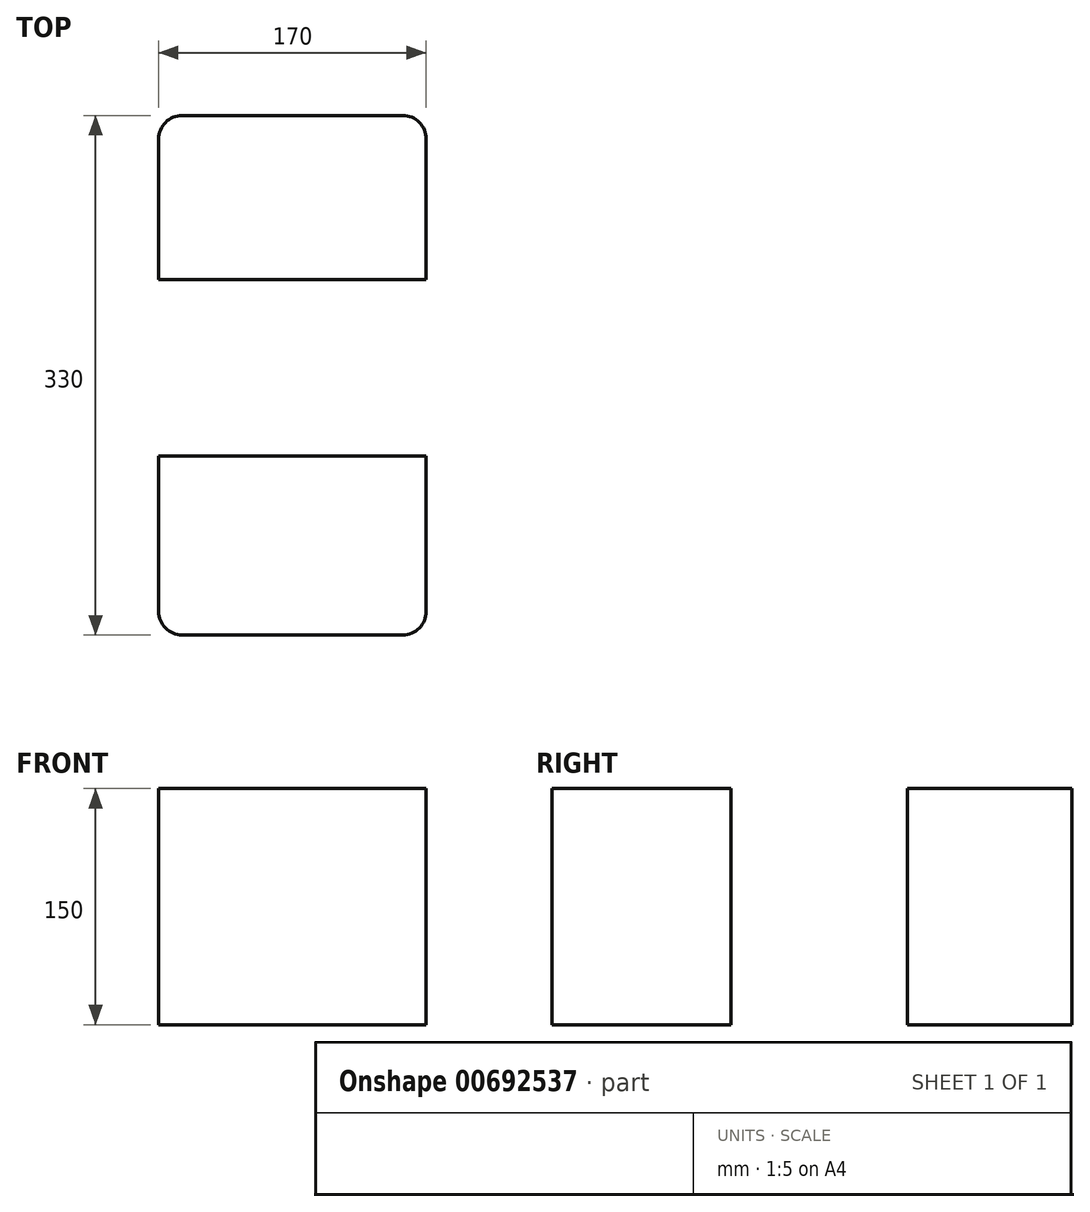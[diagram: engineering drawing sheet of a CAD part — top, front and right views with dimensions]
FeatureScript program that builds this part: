
annotation { "Feature Type Name" : "Feature", "Feature Type Description" : "" }
export const myFeature = defineFeature(function(context is Context, id is Id, definition is map)
    precondition{}
    {
        {
            var Q0;
            Q0=qCreatedBy(makeId("Top.planeOp"),FACE);
            var sketch = newSketch(context, id + "F0", { "sketchPlane" : qUnion([Q0])});
            skLineSegment(sketch, "E0.bottom", {"start": v(-226.43, 161.21) * mm, "end": v(-86.43, 161.21) * mm});
            skLineSegment(sketch, "E0.top", {"start": v(-226.43, -168.79) * mm, "end": v(-86.43, -168.79) * mm});
            skLineSegment(sketch, "E0.left", {"start": v(-241.43, 146.21) * mm, "end": v(-241.43, -153.79) * mm});
            skLineSegment(sketch, "E0.right", {"start": v(-71.43, 146.21) * mm, "end": v(-71.43, -153.79) * mm});
            skPoint(sketch, "E1.visualSharp", {"position": v(-241.43, 161.21) * mm});
            skArc(sketch, "E1.filletArc", {"start": v(-226.43, 161.21) * mm, "mid": v(-237.03, 156.82) * mm, "end": v(-241.43, 146.21) * mm});
            skPoint(sketch, "E2.visualSharp", {"position": v(-71.43, 161.21) * mm});
            skArc(sketch, "E2.filletArc", {"start": v(-71.43, 146.21) * mm, "mid": v(-75.82, 156.82) * mm, "end": v(-86.43, 161.21) * mm});
            skPoint(sketch, "E3.visualSharp", {"position": v(-71.43, -168.79) * mm});
            skArc(sketch, "E3.filletArc", {"start": v(-86.43, -168.79) * mm, "mid": v(-75.82, -164.4) * mm, "end": v(-71.43, -153.79) * mm});
            skPoint(sketch, "E4.visualSharp", {"position": v(-241.43, -168.79) * mm});
            skArc(sketch, "E4.filletArc", {"start": v(-241.43, -153.79) * mm, "mid": v(-237.03, -164.4) * mm, "end": v(-226.43, -168.79) * mm});
            skFitSpline(sketch, "E5", {"points": [v(-71.43, 68.15) * mm, v(-3.2, 106.28) * mm, v(113.73, 101.36) * mm, v(175.87, 33.67) * mm, v(184, 0) * mm], "startDerivative": vector(108.48, -37.28) * mm, "endDerivative": vector(9.77, -146.99) * mm});
            skLineSegment(sketch, "E6", {"start": v(-29.23, 0) * mm, "end": v(209.65, 0) * mm, "construction": true});
            skFitSpline(sketch, "E7.MirrorCS", {"points": [v(-71.43, -68.15) * mm, v(-3.2, -106.28) * mm, v(113.73, -101.36) * mm, v(175.87, -33.67) * mm, v(184, 0) * mm], "startDerivative": vector(108.48, 37.28) * mm, "endDerivative": vector(9.77, 146.99) * mm});
            skLineSegment(sketch, "E8.bottom", {"start": v(-241.43, 56.9) * mm, "end": v(71.66, 56.9) * mm});
            skLineSegment(sketch, "E8.top", {"start": v(-241.43, -55.18) * mm, "end": v(71.66, -55.18) * mm});
            skLineSegment(sketch, "E8.left", {"start": v(-241.43, 56.9) * mm, "end": v(-241.43, -55.18) * mm});
            skLineSegment(sketch, "E8.right", {"start": v(121.66, 6.9) * mm, "end": v(121.66, -5.18) * mm});
            skPoint(sketch, "E9.visualSharp", {"position": v(121.66, 56.9) * mm});
            skArc(sketch, "E9.filletArc", {"start": v(121.66, 6.9) * mm, "mid": v(107.01, 42.26) * mm, "end": v(71.66, 56.9) * mm});
            skPoint(sketch, "E10.visualSharp", {"position": v(121.66, -55.18) * mm});
            skArc(sketch, "E10.filletArc", {"start": v(71.66, -55.18) * mm, "mid": v(107.01, -40.53) * mm, "end": v(121.66, -5.18) * mm});
            skSolve(sketch);
        }
        {
            var Q0;
            Q0=makeQuery(id+"F0.imprint","IMPRINT",FACE,{"disambiguationData":[TD([[makeQuery(id+"F0.imprint","IMPRINT",EDGE,{"derivedFrom":sQuery(id+"F0.wireOp",EDGE,"E0.top")}),1.0]])]});
            var Q1;
            {var subQ5=sQuery(id+"F0.wireOp",EDGE,"E8.left");Q1=makeQuery(id+"F0.imprint","IMPRINT",FACE,{"disambiguationData":[TD([[makeQuery(id+"F0.imprint","IMPRINT",EDGE,{"derivedFrom":subQ5}),1.0]])]});}
            var Q2;
            Q2=makeQuery(id+"F0.imprint","IMPRINT",FACE,{"disambiguationData":[TD([[makeQuery(id+"F0.imprint","IMPRINT",EDGE,{"derivedFrom":sQuery(id+"F0.wireOp",EDGE,"E0.bottom")}),-1.0]])]});
            extrude(context, id + "F1", {"entities" : qUnion([Q0, Q1, Q2]), "depth" : 150 * mm, "offsetDistance" : 25 * mm});
        }
    });
